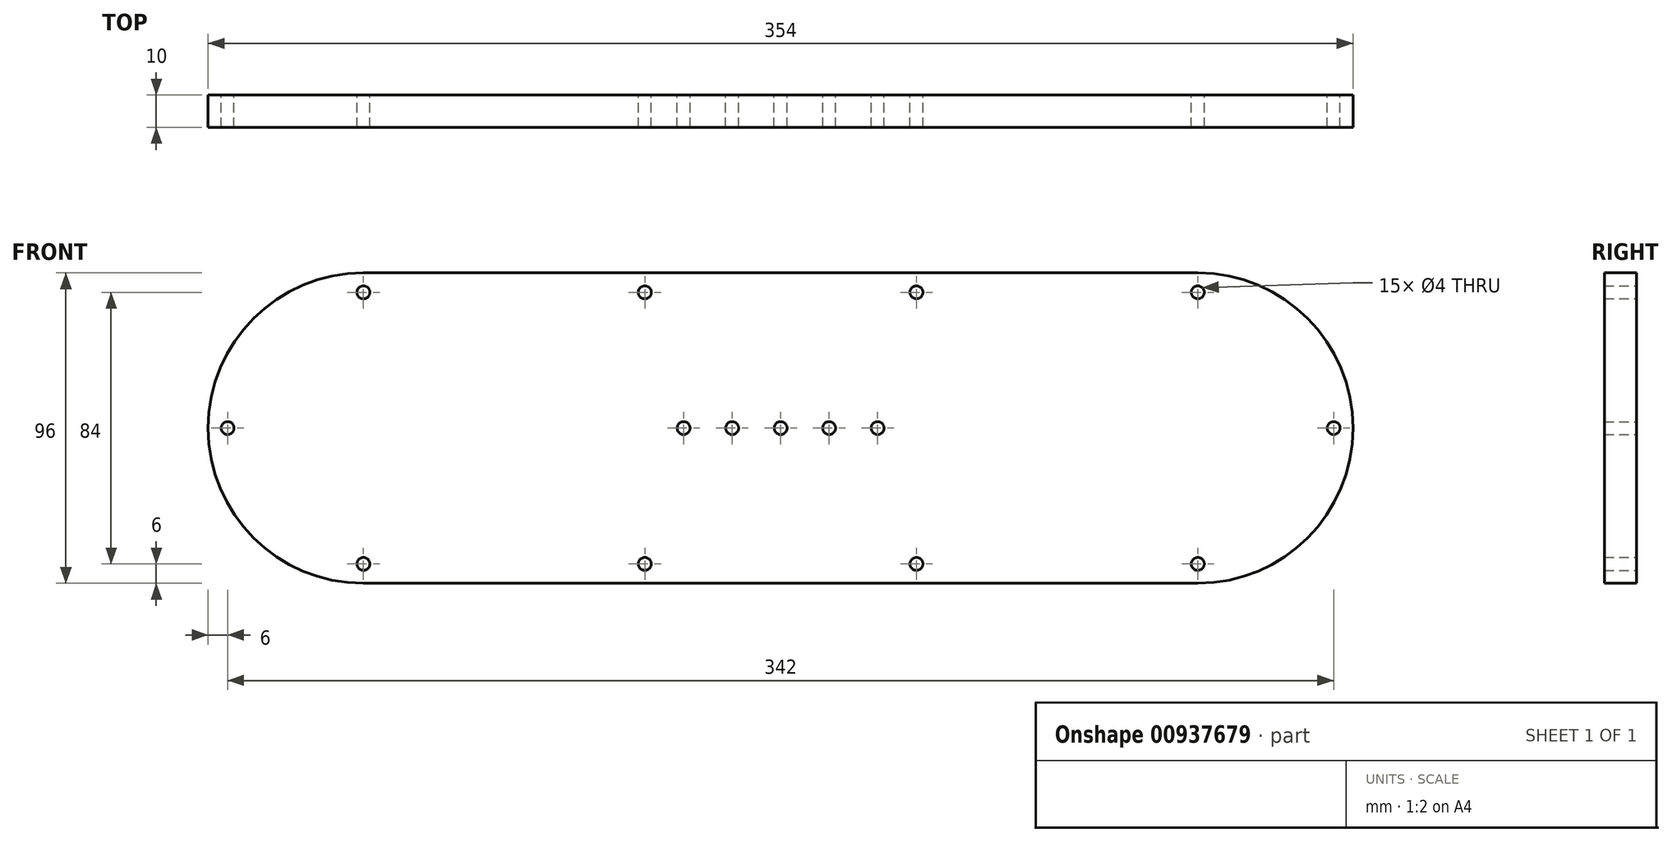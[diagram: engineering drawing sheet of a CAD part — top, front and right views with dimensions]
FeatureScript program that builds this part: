
annotation { "Feature Type Name" : "Feature", "Feature Type Description" : "" }
export const myFeature = defineFeature(function(context is Context, id is Id, definition is map)
    precondition{}
    {
        {
            var Q0;
            Q0=qCreatedBy(makeId("Front.planeOp"),FACE);
            var sketch = newSketch(context, id + "F0", { "sketchPlane" : qUnion([Q0])});
            skLineSegment(sketch, "E0", {"start": v(0, -113.77) * mm, "end": v(0, 113.17) * mm, "construction": true});
            skArc(sketch, "E1", {"start": v(129, 48) * mm, "mid": v(177, 0) * mm, "end": v(129, -48) * mm});
            skLineSegment(sketch, "E2", {"start": v(129, -48) * mm, "end": v(0, -48) * mm});
            skLineSegment(sketch, "E3", {"start": v(129, 48) * mm, "end": v(0, 48) * mm});
            skLineSegment(sketch, "E4.MirrorCS", {"start": v(-129, -48) * mm, "end": v(0, -48) * mm});
            skLineSegment(sketch, "E5.MirrorCS", {"start": v(-129, 48) * mm, "end": v(0, 48) * mm});
            skArc(sketch, "E6.MirrorCS", {"start": v(-129, 48) * mm, "mid": v(-177, 0) * mm, "end": v(-129, -48) * mm});
            skCircle(sketch, "E7", {"center": v(15, 0) * mm, "radius": 2 * mm});
            skCircle(sketch, "E8", {"center": v(30, 0) * mm, "radius": 2 * mm});
            skCircle(sketch, "E9.MirrorC", {"center": v(-30, 0) * mm, "radius": 2 * mm});
            skCircle(sketch, "E10.MirrorC", {"center": v(-15, 0) * mm, "radius": 2 * mm});
            skCircle(sketch, "E11", {"center": v(129, 42) * mm, "radius": 2 * mm});
            skCircle(sketch, "E12.2.0", {"center": v(129, -42) * mm, "radius": 2 * mm});
            skCircle(sketch, "E12.3.0", {"center": v(171, 0) * mm, "radius": 2 * mm});
            skCircle(sketch, "E13.MirrorC", {"center": v(-171, 0) * mm, "radius": 2 * mm});
            skCircle(sketch, "E14.MirrorC", {"center": v(-129, 42) * mm, "radius": 2 * mm});
            skCircle(sketch, "E15.MirrorC", {"center": v(-129, -42) * mm, "radius": 2 * mm});
            skCircle(sketch, "E16", {"center": v(42, 42) * mm, "radius": 2 * mm});
            skCircle(sketch, "E17.1.0", {"center": v(42, -42) * mm, "radius": 2 * mm});
            skCircle(sketch, "E18.MirrorC", {"center": v(-42, 42) * mm, "radius": 2 * mm});
            skCircle(sketch, "E19.MirrorC", {"center": v(-42, -42) * mm, "radius": 2 * mm});
            skCircle(sketch, "E20", {"center": v(0, 0) * mm, "radius": 2 * mm});
            skSolve(sketch);
        }
        {
            var Q0;
            Q0=qSketchRegion(id+"F0",true);
            extrude(context, id + "F1", {"entities" : qUnion([Q0]), "depth" : 10 * mm, "offsetDistance" : 25 * mm});
        }
    });
